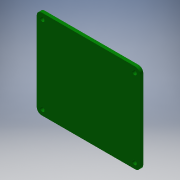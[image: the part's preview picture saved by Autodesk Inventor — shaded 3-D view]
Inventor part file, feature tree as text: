
AUTODESK INVENTOR PART (.ipt)
format: ipt  version: 2018 (Build 220112000, 112)  size: 110,080 bytes
history: native  units: in
note: dims shown in document units (in); Inventor stores cm internally (conversion verified against a paired STEP export)
features: other x7, reference x4, extrude x2, sketch x2
ambient origin geometry x8: Origin, YZ Plane, XZ Plane, XY Plane, X Axis, Y Axis, Z Axis, Center Point
bodies: Solid1 (feature_tree)
feature tree (15):
  extrude  "Extrusion1"  Depth=2.2047in
  extrude  "Extrusion2"  Depth=0.0787in
  sketch  "Sketch1"  dims[d0=2.5591in d1=2.2047in]
  sketch  "Sketch2"  dims[d2=1.1024in d3=1.2795in d4=0.1181in d5=0.0787in d6=0.0in d7=0.0787in d8=0.0in]
  reference  "Reference1"
  reference  "Reference2"
  reference  "Reference3"
  reference  "Reference4"
  other  "<userpath>\Desktop\LocalGit\seniorproject\hardware\mechanical\Hub\Hub Assembly.iam"
  other  "Hub Assembly.iam"
  other  "Raspberry Pi 3:1"
  other  "Raspberry Pi 345_533"
  other  "Raspberry Pi 345_532"
  other  "Raspberry Pi 345_531"
  other  "Raspberry Pi 345_530"
